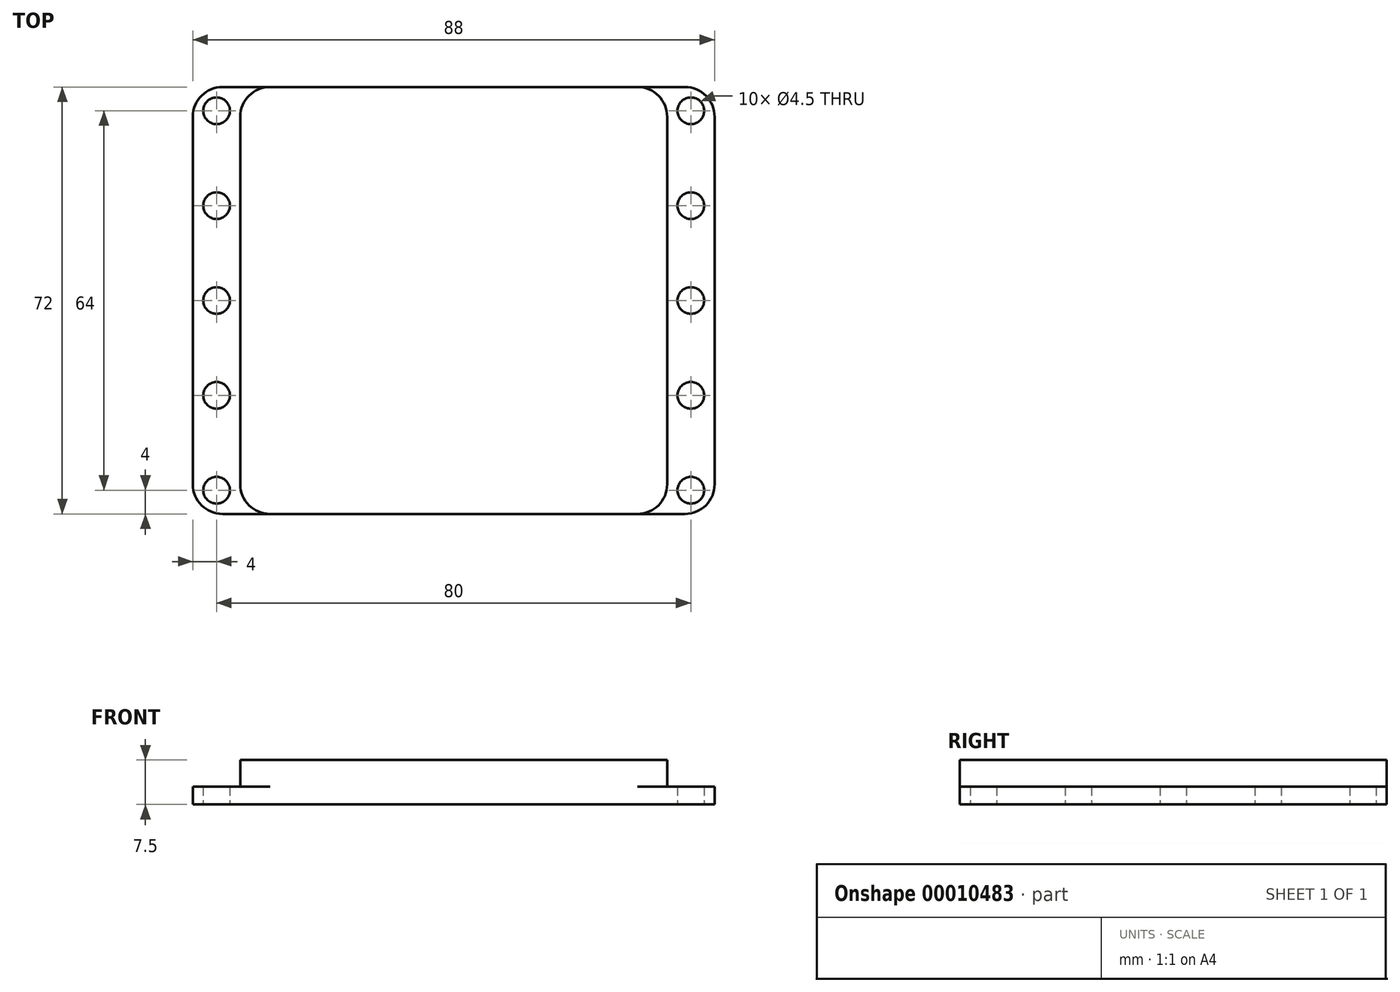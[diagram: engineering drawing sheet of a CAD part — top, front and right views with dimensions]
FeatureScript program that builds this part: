
annotation { "Feature Type Name" : "Feature", "Feature Type Description" : "" }
export const myFeature = defineFeature(function(context is Context, id is Id, definition is map)
    precondition{}
    {
        {
            var Q0;
            Q0=qCreatedBy(makeId("Front.planeOp"),FACE);
            var sketch = newSketch(context, id + "F0", { "sketchPlane" : qUnion([Q0])});
            skPoint(sketch, "E0.rect.middle", {"position": v(44, 3) * mm});
            skPoint(sketch, "E1.orphan", {"position": v(80, -1.5) * mm});
            skPoint(sketch, "E2.orphan", {"position": v(8, -1.5) * mm});
            skLineSegment(sketch, "E3.bottom", {"start": v(0, 0) * mm, "end": v(88, 0) * mm});
            skLineSegment(sketch, "E0.rect.bottom", {"start": v(80, 7.5) * mm, "end": v(8, 7.5) * mm});
            skLineSegment(sketch, "E4.trimOffspring", {"start": v(80, 3) * mm, "end": v(88, 3) * mm});
            skLineSegment(sketch, "E3.top", {"start": v(0, 3) * mm, "end": v(8, 3) * mm});
            skLineSegment(sketch, "E0.rect.left", {"start": v(80, 7.5) * mm, "end": v(80, 3) * mm});
            skLineSegment(sketch, "E3.left", {"start": v(0, 0) * mm, "end": v(0, 3) * mm});
            skLineSegment(sketch, "E3.right", {"start": v(88, 0) * mm, "end": v(88, 3) * mm});
            skLineSegment(sketch, "E0.rect.right", {"start": v(8, 7.5) * mm, "end": v(8, 3) * mm});
            skSolve(sketch);
        }
        {
            var Q0;
            Q0=makeQuery(id+"F0.imprint","IMPRINT",FACE,{"disambiguationData":[TD([[makeQuery(id+"F0.imprint","IMPRINT",EDGE,{"derivedFrom":sQuery(id+"F0.wireOp",EDGE,"E3.bottom")}),1.0]])]});
            extrude(context, id + "F1", {"entities" : qUnion([Q0]), "depth" : 72 * mm});
        }
        {
            var Q0;
            Q0=makeQuery(id+"F1.opExtrude","CAP_EDGE",EDGE,{"disambiguationData":[OSD([sQuery(id+"F0.wireOp",EDGE,"E0.rect.right")])],"isStart":false});
            var Q1;
            Q1=makeQuery(id+"F1.opExtrude","CAP_EDGE",EDGE,{"disambiguationData":[OSD([sQuery(id+"F0.wireOp",EDGE,"E0.rect.left")])],"isStart":false});
            var Q2;
            Q2=makeQuery(id+"F1.opExtrude","CAP_EDGE",EDGE,{"disambiguationData":[OSD([sQuery(id+"F0.wireOp",EDGE,"E0.rect.left")])],"isStart":true});
            var Q3;
            Q3=makeQuery(id+"F1.opExtrude","CAP_EDGE",EDGE,{"disambiguationData":[OSD([sQuery(id+"F0.wireOp",EDGE,"E0.rect.right")])],"isStart":true});
            var Q4;
            Q4=makeQuery(id+"F1.opExtrude","CAP_EDGE",EDGE,{"disambiguationData":[OSD([sQuery(id+"F0.wireOp",EDGE,"E3.right")])],"isStart":false});
            var Q5;
            Q5=makeQuery(id+"F1.opExtrude","CAP_EDGE",EDGE,{"disambiguationData":[OSD([sQuery(id+"F0.wireOp",EDGE,"E3.right")])],"isStart":true});
            var Q6;
            Q6=makeQuery(id+"F1.opExtrude","CAP_EDGE",EDGE,{"disambiguationData":[OSD([sQuery(id+"F0.wireOp",EDGE,"E3.left")])],"isStart":true});
            var Q7;
            Q7=makeQuery(id+"F1.opExtrude","CAP_EDGE",EDGE,{"disambiguationData":[OSD([sQuery(id+"F0.wireOp",EDGE,"E3.left")])],"isStart":false});
            fillet(context, id + "F2", {"entities" : qUnion([Q0, Q1, Q2, Q3, Q4, Q5, Q6, Q7]), "radius" : 5 * mm, "tangentPropagation" : true, "allowEdgeOverflow" : false});
        }
        {
            var Q0;
            Q0=makeQuery(id+"F1.opExtrude","SWEPT_FACE",FACE,{"disambiguationData":[OSD([sQuery(id+"F0.wireOp",EDGE,"E3.bottom")])]});
            var sketch = newSketch(context, id + "F3", { "sketchPlane" : qUnion([Q0])});
            skLineSegment(sketch, "E5.direction2", {"start": v(4, 68) * mm, "end": v(4, 52) * mm, "construction": true});
            skCircle(sketch, "E5.1.3.0", {"center": v(84, 20) * mm, "radius": 2.25 * mm});
            skCircle(sketch, "E5.1.4.0", {"center": v(84, 4) * mm, "radius": 2.25 * mm});
            skCircle(sketch, "E5.1.1.0", {"center": v(84, 52) * mm, "radius": 2.25 * mm});
            skCircle(sketch, "E5.1.2.0", {"center": v(84, 36) * mm, "radius": 2.25 * mm});
            skCircle(sketch, "E5.1.0.0", {"center": v(84, 68) * mm, "radius": 2.25 * mm});
            skLineSegment(sketch, "E5.direction1", {"start": v(4, 68) * mm, "end": v(84, 68) * mm, "construction": true});
            skCircle(sketch, "E5.0.4.0", {"center": v(4, 4) * mm, "radius": 2.25 * mm});
            skCircle(sketch, "E5.0.3.0", {"center": v(4, 20) * mm, "radius": 2.25 * mm});
            skCircle(sketch, "E5.0.2.0", {"center": v(4, 36) * mm, "radius": 2.25 * mm});
            skCircle(sketch, "E5.0.1.0", {"center": v(4, 52) * mm, "radius": 2.25 * mm});
            skCircle(sketch, "E6", {"center": v(4, 68) * mm, "radius": 2.25 * mm});
            skLineSegment(sketch, "E7", {"start": v(44, 72) * mm, "end": v(44, 0) * mm, "construction": true});
            skSolve(sketch);
        }
        {
            var Q0;
            Q0 = qSketchRegion(id + "F3", true);
            extrude(context, id + "F4", {"entities" : qUnion([Q0]), "operationType" : NewBodyOperationType.REMOVE, "endBound" : BoundingType.UP_TO_NEXT, "oppositeDirection" : true, "depth" : 25 * mm});
        }
    });
